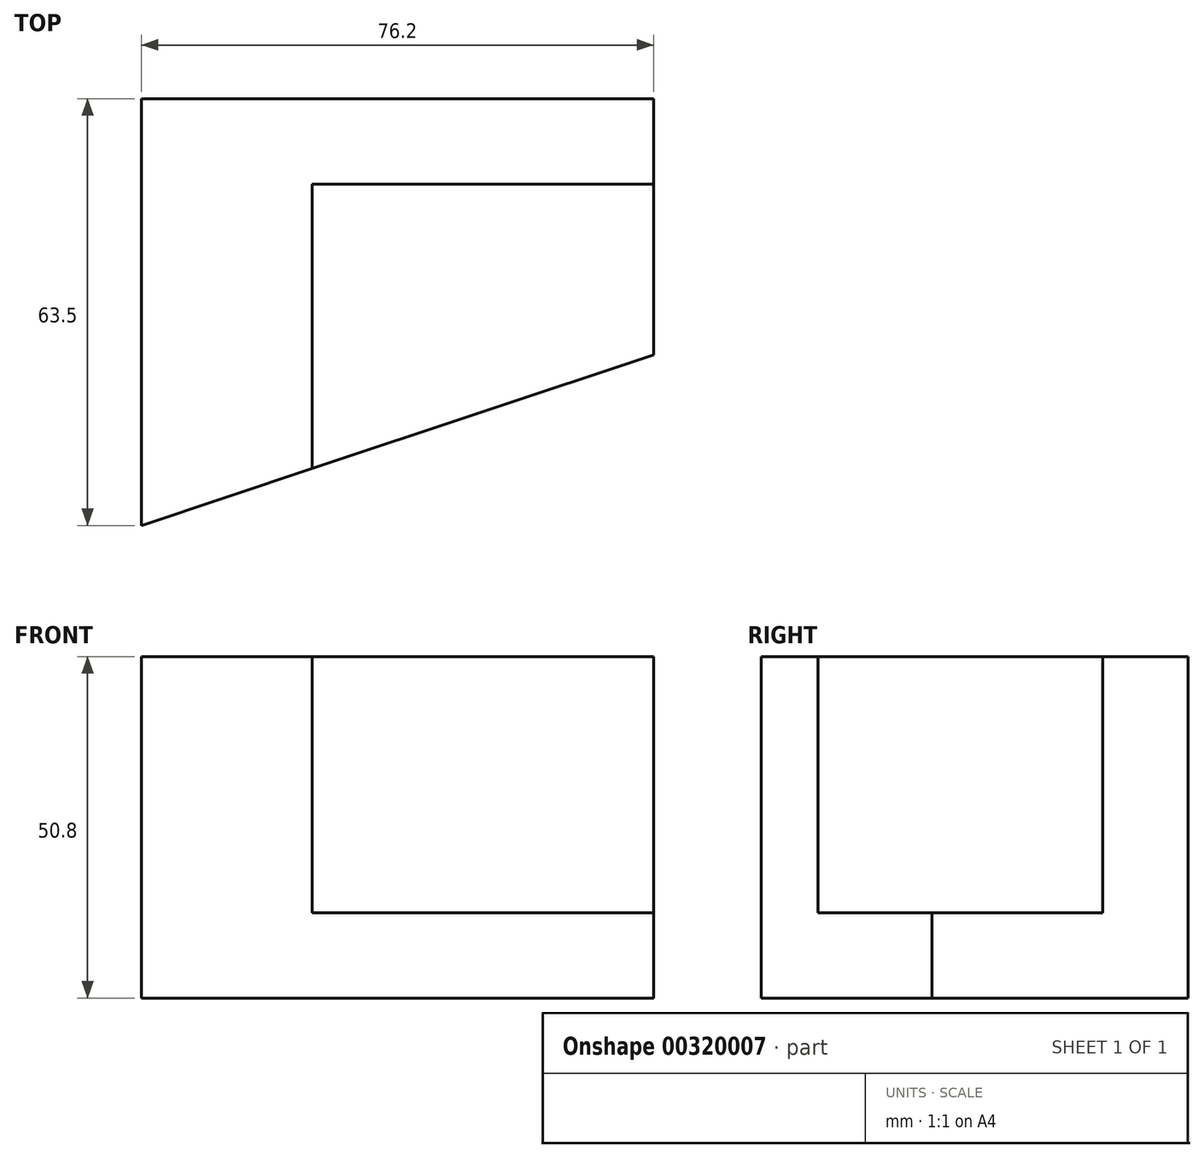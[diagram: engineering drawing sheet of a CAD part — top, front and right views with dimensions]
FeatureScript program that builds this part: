
annotation { "Feature Type Name" : "Feature", "Feature Type Description" : "" }
export const myFeature = defineFeature(function(context is Context, id is Id, definition is map)
    precondition{}
    {
        {
            var Q0;
            Q0=qCreatedBy(makeId("Front.planeOp"),FACE);
            var sketch = newSketch(context, id + "F0", { "sketchPlane" : qUnion([Q0])});
            skLineSegment(sketch, "E0.bottom", {"start": v(0, 0) * mm, "end": v(76.2, 0) * mm});
            skLineSegment(sketch, "E0.top", {"start": v(0, 50.8) * mm, "end": v(76.2, 50.8) * mm});
            skLineSegment(sketch, "E0.left", {"start": v(0, 0) * mm, "end": v(0, 50.8) * mm});
            skLineSegment(sketch, "E0.right", {"start": v(76.2, 0) * mm, "end": v(76.2, 50.8) * mm});
            skSolve(sketch);
        }
        {
            var Q0;
            Q0 = qSketchRegion(id + "F0", true);
            extrude(context, id + "F1", {"entities" : qUnion([Q0]), "oppositeDirection" : true, "depth" : 63.5 * mm});
        }
        {
            var Q0;
            Q0=makeQuery(id+"F1.opExtrude","SWEPT_FACE",FACE,{"disambiguationData":[OSD([sQuery(id+"F0.wireOp",EDGE,"E0.top")])]});
            var sketch = newSketch(context, id + "F2", { "sketchPlane" : qUnion([Q0])});
            skLineSegment(sketch, "E1", {"start": v(0, 0) * mm, "end": v(76.2, 25.4) * mm});
            skLineSegment(sketch, "E2", {"start": v(25.4, 50.8) * mm, "end": v(25.4, 8.47) * mm});
            skLineSegment(sketch, "E3", {"start": v(25.4, 50.8) * mm, "end": v(76.2, 50.8) * mm});
            skSolve(sketch);
        }
        {
            var Q0;
            {var subQ3=sQuery(id+"F2.wireOp",EDGE,"E2");Q0=makeQuery(id+"F2.imprint","IMPRINT",FACE,{"disambiguationData":[TD([[makeQuery(id+"F2.imprint","IMPRINT",EDGE,{"derivedFrom":subQ3}),1.0]])]});}
            extrude(context, id + "F3", {"entities" : qUnion([Q0]), "operationType" : NewBodyOperationType.REMOVE, "oppositeDirection" : true, "depth" : 38.1 * mm});
        }
        {
            var Q0;
            {var subQ1=sQuery(id+"F0.wireOp",EDGE,"E0.top");var subQ2=makeQuery(id+"F1.opExtrude","CAP_EDGE",EDGE,{"disambiguationData":[OSD([subQ1])],"isStart":true});Q0=makeQuery(id+"F2.imprint","IMPRINT",FACE,{"disambiguationData":[TD([[makeQuery(id+"F2.imprint","IMPRINT",EDGE,{"derivedFrom":subQ2}),1.0]])]});}
            extrude(context, id + "F4", {"entities" : qUnion([Q0]), "operationType" : NewBodyOperationType.REMOVE, "oppositeDirection" : true, "depth" : 76.2 * mm});
        }
    });
